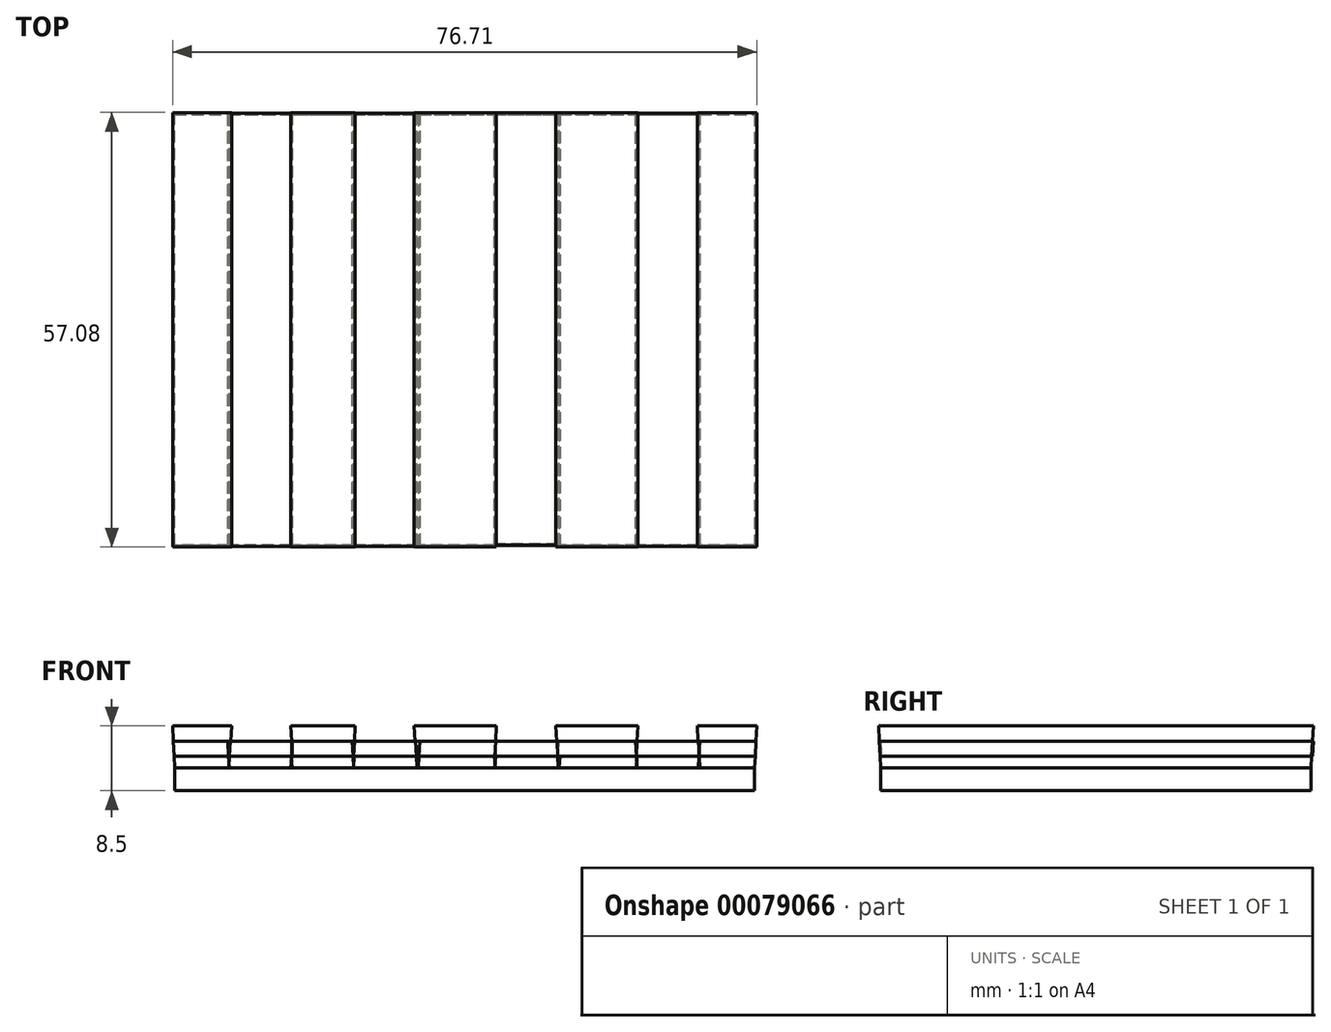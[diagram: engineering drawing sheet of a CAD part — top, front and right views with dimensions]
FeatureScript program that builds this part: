
annotation { "Feature Type Name" : "Feature", "Feature Type Description" : "" }
export const myFeature = defineFeature(function(context is Context, id is Id, definition is map)
    precondition{}
    {
        {
            var Q0;
            Q0=qCreatedBy(makeId("Top.planeOp"),FACE);
            var sketch = newSketch(context, id + "F0", { "sketchPlane" : qUnion([Q0])});
            skLineSegment(sketch, "E0.bottom", {"start": v(-76.14, 56.5) * mm, "end": v(0, 56.5) * mm});
            skLineSegment(sketch, "E0.top", {"start": v(-76.14, 0) * mm, "end": v(0, 0) * mm});
            skLineSegment(sketch, "E0.left", {"start": v(-76.14, 56.5) * mm, "end": v(-76.14, 0) * mm});
            skLineSegment(sketch, "E0.right", {"start": v(0, 56.5) * mm, "end": v(0, 0) * mm});
            skSolve(sketch);
        }
        {
            var Q0;
            Q0=qSketchRegion(id+"F0",true);
            extrude(context, id + "F1", {"entities" : qUnion([Q0]), "depth" : 3 * mm});
        }
        {
            var Q0;
            Q0=makeQuery(id+"F1.opExtrude","CAP_FACE",FACE,{"disambiguationData":[OSD([sQuery(id+"F0.wireOp",EDGE,"E0.bottom"),sQuery(id+"F0.wireOp",EDGE,"E0.top"),sQuery(id+"F0.wireOp",EDGE,"E0.left"),sQuery(id+"F0.wireOp",EDGE,"E0.right")])],"isStart":false});
            var sketch = newSketch(context, id + "F2", { "sketchPlane" : qUnion([Q0])});
            skLineSegment(sketch, "E1.bottom", {"start": v(-76.14, 56.5) * mm, "end": v(0, 56.5) * mm});
            skLineSegment(sketch, "E1.top", {"start": v(-76.14, 0) * mm, "end": v(0, 0) * mm});
            skLineSegment(sketch, "E1.left", {"start": v(-76.14, 56.5) * mm, "end": v(-76.14, 0) * mm});
            skLineSegment(sketch, "E1.right", {"start": v(0, 56.5) * mm, "end": v(0, 0) * mm});
            skSolve(sketch);
        }
        {
            var Q0;
            Q0=makeQuery(id+"F2.imprint","IMPRINT",FACE,{"disambiguationData":[TD([[makeQuery(id+"F2.imprint","IMPRINT",EDGE,{"derivedFrom":sQuery(id+"F2.wireOp",EDGE,"E1.bottom")}),-1.0]])]});
            extrude(context, id + "F3", {"entities" : qUnion([Q0]), "depth" : 1.5 * mm, "hasDraft" : true, "draftAngle" : 3 * degree});
        }
        {
            var Q0;
            Q0=makeQuery(id+"F3.opExtrude","CAP_FACE",FACE,{"disambiguationData":[OSD([sQuery(id+"F2.wireOp",EDGE,"E1.bottom"),sQuery(id+"F2.wireOp",EDGE,"E1.top"),sQuery(id+"F2.wireOp",EDGE,"E1.left"),sQuery(id+"F2.wireOp",EDGE,"E1.right")])],"isStart":false});
            var sketch = newSketch(context, id + "F4", { "sketchPlane" : qUnion([Q0])});
            skLineSegment(sketch, "E2.bottom", {"start": v(-76.22, 56.58) * mm, "end": v(0.08, 56.58) * mm});
            skLineSegment(sketch, "E2.top", {"start": v(-76.22, -0.08) * mm, "end": v(0.08, -0.08) * mm});
            skLineSegment(sketch, "E2.left", {"start": v(-76.22, 56.58) * mm, "end": v(-76.22, -0.08) * mm});
            skLineSegment(sketch, "E2.right", {"start": v(0.08, 56.58) * mm, "end": v(0.08, -0.08) * mm});
            skSolve(sketch);
        }
        {
            var Q0;
            Q0=qSketchRegion(id+"F4",true);
            extrude(context, id + "F5", {"entities" : qUnion([Q0]), "depth" : 2 * mm, "hasDraft" : true, "draftAngle" : 3 * degree});
        }
        {
            var Q0;
            Q0=makeQuery(id+"F5.opExtrude","CAP_FACE",FACE,{"disambiguationData":[OSD([sQuery(id+"F4.wireOp",EDGE,"E2.bottom"),sQuery(id+"F4.wireOp",EDGE,"E2.top"),sQuery(id+"F4.wireOp",EDGE,"E2.left"),sQuery(id+"F4.wireOp",EDGE,"E2.right")])],"isStart":false});
            var sketch = newSketch(context, id + "F6", { "sketchPlane" : qUnion([Q0])});
            skLineSegment(sketch, "E3.bottom", {"start": v(-68.76, 56.68) * mm, "end": v(-60.82, 56.68) * mm});
            skLineSegment(sketch, "E3.top", {"start": v(-68.76, -0.18) * mm, "end": v(-60.82, -0.18) * mm});
            skLineSegment(sketch, "E3.left", {"start": v(-68.76, 56.68) * mm, "end": v(-68.76, -0.18) * mm});
            skLineSegment(sketch, "E3.right", {"start": v(-60.82, 56.68) * mm, "end": v(-60.82, -0.18) * mm});
            skSolve(sketch);
        }
        {
            var Q0;
            Q0=qSketchRegion(id+"F6",true);
            extrude(context, id + "F7", {"entities" : qUnion([Q0]), "operationType" : NewBodyOperationType.REMOVE, "oppositeDirection" : true, "depth" : 2 * mm, "hasDraft" : true, "draftAngle" : 3 * degree});
        }
        {
            var Q0;
            {var subQ0=sQuery(id+"F4.wireOp",EDGE,"E2.bottom");var subQ1=sQuery(id+"F4.wireOp",EDGE,"E2.top");var subQ2=sQuery(id+"F4.wireOp",EDGE,"E2.right");Q0=makeQuery(id+"F7.boolean.opBoolean","SPLIT",FACE,{"disambiguationData":[TD([makeQuery(id+"F5.opExtrude","SWEPT_FACE",FACE,{"disambiguationData":[OSD([subQ2])]})])],"derivedFrom":makeQuery(id+"F5.opExtrude","CAP_FACE",FACE,{"disambiguationData":[OSD([subQ0,subQ1,sQuery(id+"F4.wireOp",EDGE,"E2.left"),subQ2])],"isStart":false})});}
            var sketch = newSketch(context, id + "F8", { "sketchPlane" : qUnion([Q0])});
            skLineSegment(sketch, "E4.bottom", {"start": v(-52.56, 56.68) * mm, "end": v(-44.62, 56.68) * mm});
            skLineSegment(sketch, "E4.top", {"start": v(-52.56, -0.18) * mm, "end": v(-44.62, -0.18) * mm});
            skLineSegment(sketch, "E4.left", {"start": v(-52.56, 56.68) * mm, "end": v(-52.56, -0.18) * mm});
            skLineSegment(sketch, "E4.right", {"start": v(-44.62, 56.68) * mm, "end": v(-44.62, -0.18) * mm});
            skSolve(sketch);
        }
        {
            var Q0;
            Q0=qSketchRegion(id+"F8",true);
            extrude(context, id + "F9", {"entities" : qUnion([Q0]), "operationType" : NewBodyOperationType.REMOVE, "oppositeDirection" : true, "depth" : 2 * mm, "hasDraft" : true, "draftAngle" : 3 * degree});
        }
        {
            var Q0;
            {var subQ0=sQuery(id+"F4.wireOp",EDGE,"E2.bottom");var subQ2=sQuery(id+"F4.wireOp",EDGE,"E2.top");var subQ4=sQuery(id+"F4.wireOp",EDGE,"E2.right");var subQ5=makeQuery(id+"F5.opExtrude","SWEPT_FACE",FACE,{"disambiguationData":[OSD([subQ4])]});Q0=makeQuery(id+"F9.boolean.opBoolean","SPLIT",FACE,{"disambiguationData":[TD([subQ5])],"derivedFrom":makeQuery(id+"F7.boolean.opBoolean","SPLIT",FACE,{"disambiguationData":[TD([subQ5])],"derivedFrom":makeQuery(id+"F5.opExtrude","CAP_FACE",FACE,{"disambiguationData":[OSD([subQ0,subQ2,sQuery(id+"F4.wireOp",EDGE,"E2.left"),subQ4])],"isStart":false})})});}
            var sketch = newSketch(context, id + "F10", { "sketchPlane" : qUnion([Q0])});
            skLineSegment(sketch, "E5.bottom", {"start": v(-34, 56.68) * mm, "end": v(-25.99, 56.68) * mm});
            skLineSegment(sketch, "E5.top", {"start": v(-34, -0.18) * mm, "end": v(-25.99, -0.18) * mm});
            skLineSegment(sketch, "E5.left", {"start": v(-34, 56.68) * mm, "end": v(-34, -0.18) * mm});
            skLineSegment(sketch, "E5.right", {"start": v(-25.99, 56.68) * mm, "end": v(-25.99, -0.18) * mm});
            skSolve(sketch);
        }
        {
            var Q0;
            Q0=qSketchRegion(id+"F10",true);
            extrude(context, id + "F11", {"entities" : qUnion([Q0]), "operationType" : NewBodyOperationType.REMOVE, "oppositeDirection" : true, "depth" : 2 * mm, "hasDraft" : true, "draftAngle" : 3 * degree});
        }
        {
            var Q0;
            {var subQ0=sQuery(id+"F4.wireOp",EDGE,"E2.bottom");var subQ2=sQuery(id+"F4.wireOp",EDGE,"E2.top");var subQ4=sQuery(id+"F4.wireOp",EDGE,"E2.right");var subQ5=makeQuery(id+"F5.opExtrude","SWEPT_FACE",FACE,{"disambiguationData":[OSD([subQ4])]});Q0=makeQuery(id+"F11.boolean.opBoolean","SPLIT",FACE,{"disambiguationData":[TD([subQ5])],"derivedFrom":makeQuery(id+"F9.boolean.opBoolean","SPLIT",FACE,{"disambiguationData":[TD([subQ5])],"derivedFrom":makeQuery(id+"F7.boolean.opBoolean","SPLIT",FACE,{"disambiguationData":[TD([subQ5])],"derivedFrom":makeQuery(id+"F5.opExtrude","CAP_FACE",FACE,{"disambiguationData":[OSD([subQ0,subQ2,sQuery(id+"F4.wireOp",EDGE,"E2.left"),subQ4])],"isStart":false})})})});}
            var sketch = newSketch(context, id + "F12", { "sketchPlane" : qUnion([Q0])});
            skLineSegment(sketch, "E6.bottom", {"start": v(-15.44, 56.68) * mm, "end": v(-7.42, 56.68) * mm});
            skLineSegment(sketch, "E6.top", {"start": v(-15.44, -0.18) * mm, "end": v(-7.42, -0.18) * mm});
            skLineSegment(sketch, "E6.left", {"start": v(-15.44, 56.68) * mm, "end": v(-15.44, -0.18) * mm});
            skLineSegment(sketch, "E6.right", {"start": v(-7.42, 56.68) * mm, "end": v(-7.42, -0.18) * mm});
            skSolve(sketch);
        }
        {
            var Q0;
            Q0=qSketchRegion(id+"F12",true);
            extrude(context, id + "F13", {"entities" : qUnion([Q0]), "operationType" : NewBodyOperationType.REMOVE, "oppositeDirection" : true, "depth" : 2 * mm, "hasDraft" : true, "draftAngle" : 3 * degree});
        }
        {
            var Q0;
            {var subQ0=sQuery(id+"F4.wireOp",EDGE,"E2.bottom");var subQ1=sQuery(id+"F4.wireOp",EDGE,"E2.top");var subQ2=sQuery(id+"F4.wireOp",EDGE,"E2.left");Q0=makeQuery(id+"F7.boolean.opBoolean","SPLIT",FACE,{"disambiguationData":[TD([makeQuery(id+"F5.opExtrude","SWEPT_FACE",FACE,{"disambiguationData":[OSD([subQ2])]})])],"derivedFrom":makeQuery(id+"F5.opExtrude","CAP_FACE",FACE,{"disambiguationData":[OSD([subQ0,subQ1,subQ2,sQuery(id+"F4.wireOp",EDGE,"E2.right")])],"isStart":false})});}
            var sketch = newSketch(context, id + "F14", { "sketchPlane" : qUnion([Q0])});
            skLineSegment(sketch, "E7.bottom", {"start": v(-76.32, 56.68) * mm, "end": v(-68.76, 56.68) * mm});
            skLineSegment(sketch, "E7.top", {"start": v(-76.32, -0.18) * mm, "end": v(-68.76, -0.18) * mm});
            skLineSegment(sketch, "E7.left", {"start": v(-76.32, 56.68) * mm, "end": v(-76.32, -0.18) * mm});
            skLineSegment(sketch, "E7.right", {"start": v(-68.76, 56.68) * mm, "end": v(-68.76, -0.18) * mm});
            skSolve(sketch);
        }
        {
            var Q0;
            Q0=qSketchRegion(id+"F14",true);
            extrude(context, id + "F15", {"entities" : qUnion([Q0]), "depth" : 2 * mm, "hasDraft" : true, "draftAngle" : 3 * degree});
        }
        {
            var Q0;
            {var subQ0=sQuery(id+"F4.wireOp",EDGE,"E2.bottom");var subQ2=sQuery(id+"F4.wireOp",EDGE,"E2.top");var subQ4=makeQuery(id+"F7.opExtrude","SWEPT_FACE",FACE,{"disambiguationData":[OSD([sQuery(id+"F6.wireOp",EDGE,"E3.right")])]});var subQ5=sQuery(id+"F4.wireOp",EDGE,"E2.right");Q0=makeQuery(id+"F9.boolean.opBoolean","SPLIT",FACE,{"disambiguationData":[TD([makeQuery(id+"F7.boolean.opBoolean","COPY",FACE,{"derivedFrom":subQ4})])],"derivedFrom":makeQuery(id+"F7.boolean.opBoolean","SPLIT",FACE,{"disambiguationData":[TD([makeQuery(id+"F5.opExtrude","SWEPT_FACE",FACE,{"disambiguationData":[OSD([subQ5])]})])],"derivedFrom":makeQuery(id+"F5.opExtrude","CAP_FACE",FACE,{"disambiguationData":[OSD([subQ0,subQ2,sQuery(id+"F4.wireOp",EDGE,"E2.left"),subQ5])],"isStart":false})})});}
            var sketch = newSketch(context, id + "F16", { "sketchPlane" : qUnion([Q0])});
            skLineSegment(sketch, "E8.bottom", {"start": v(-60.82, 56.68) * mm, "end": v(-52.56, 56.68) * mm});
            skLineSegment(sketch, "E8.top", {"start": v(-60.82, -0.18) * mm, "end": v(-52.56, -0.18) * mm});
            skLineSegment(sketch, "E8.left", {"start": v(-60.82, 56.68) * mm, "end": v(-60.82, -0.18) * mm});
            skLineSegment(sketch, "E8.right", {"start": v(-52.56, 56.68) * mm, "end": v(-52.56, -0.18) * mm});
            skSolve(sketch);
        }
        {
            var Q0;
            Q0=qSketchRegion(id+"F16",true);
            extrude(context, id + "F17", {"entities" : qUnion([Q0]), "depth" : 2 * mm, "hasDraft" : true, "draftAngle" : 3 * degree});
        }
        {
            var Q0;
            Q0=makeQuery(id+"F3.opExtrude","CAP_FACE",FACE,{"disambiguationData":[OSD([sQuery(id+"F2.wireOp",EDGE,"E1.bottom"),sQuery(id+"F2.wireOp",EDGE,"E1.top"),sQuery(id+"F2.wireOp",EDGE,"E1.left"),sQuery(id+"F2.wireOp",EDGE,"E1.right")])],"isStart":false});
            var sketch = newSketch(context, id + "F18", { "sketchPlane" : qUnion([Q0])});
            skLineSegment(sketch, "E9.bottom", {"start": v(-68.78, 56.58) * mm, "end": v(-61.04, 56.58) * mm});
            skLineSegment(sketch, "E9.top", {"start": v(-68.78, -0.08) * mm, "end": v(-61.04, -0.08) * mm});
            skLineSegment(sketch, "E9.left", {"start": v(-68.78, 56.58) * mm, "end": v(-68.78, -0.08) * mm});
            skLineSegment(sketch, "E9.right", {"start": v(-61.04, 56.58) * mm, "end": v(-61.04, -0.08) * mm});
            skSolve(sketch);
        }
        {
            var Q0;
            Q0=qSketchRegion(id+"F18",true);
            extrude(context, id + "F19", {"entities" : qUnion([Q0]), "depth" : 2 * mm, "hasDraft" : true, "draftAngle" : 3 * degree});
        }
        {
            var Q0;
            Q0=makeQuery(id+"F3.opExtrude","CAP_FACE",FACE,{"disambiguationData":[OSD([sQuery(id+"F2.wireOp",EDGE,"E1.bottom"),sQuery(id+"F2.wireOp",EDGE,"E1.top"),sQuery(id+"F2.wireOp",EDGE,"E1.left"),sQuery(id+"F2.wireOp",EDGE,"E1.right")])],"isStart":false});
            var sketch = newSketch(context, id + "F20", { "sketchPlane" : qUnion([Q0])});
            skLineSegment(sketch, "E10.bottom", {"start": v(-52.37, 56.58) * mm, "end": v(-44.62, 56.58) * mm});
            skLineSegment(sketch, "E10.top", {"start": v(-52.37, -0.08) * mm, "end": v(-44.62, -0.08) * mm});
            skLineSegment(sketch, "E10.left", {"start": v(-52.37, 56.58) * mm, "end": v(-52.37, -0.08) * mm});
            skLineSegment(sketch, "E10.right", {"start": v(-44.62, 56.58) * mm, "end": v(-44.62, -0.08) * mm});
            skSolve(sketch);
        }
        {
            var Q0;
            Q0=qSketchRegion(id+"F20",true);
            extrude(context, id + "F21", {"entities" : qUnion([Q0]), "depth" : 2 * mm, "hasDraft" : true, "draftAngle" : 3 * degree});
        }
        {
            var Q0;
            {var subQ0=sQuery(id+"F4.wireOp",EDGE,"E2.bottom");var subQ2=sQuery(id+"F4.wireOp",EDGE,"E2.top");var subQ4=makeQuery(id+"F9.opExtrude","SWEPT_FACE",FACE,{"disambiguationData":[OSD([sQuery(id+"F8.wireOp",EDGE,"E4.right")])]});var subQ5=sQuery(id+"F4.wireOp",EDGE,"E2.right");var subQ6=makeQuery(id+"F5.opExtrude","SWEPT_FACE",FACE,{"disambiguationData":[OSD([subQ5])]});Q0=makeQuery(id+"F11.boolean.opBoolean","SPLIT",FACE,{"disambiguationData":[TD([makeQuery(id+"F9.boolean.opBoolean","COPY",FACE,{"derivedFrom":subQ4})])],"derivedFrom":makeQuery(id+"F9.boolean.opBoolean","SPLIT",FACE,{"disambiguationData":[TD([subQ6])],"derivedFrom":makeQuery(id+"F7.boolean.opBoolean","SPLIT",FACE,{"disambiguationData":[TD([subQ6])],"derivedFrom":makeQuery(id+"F5.opExtrude","CAP_FACE",FACE,{"disambiguationData":[OSD([subQ0,subQ2,sQuery(id+"F4.wireOp",EDGE,"E2.left"),subQ5])],"isStart":false})})})});}
            var sketch = newSketch(context, id + "F22", { "sketchPlane" : qUnion([Q0])});
            skLineSegment(sketch, "E11.bottom", {"start": v(-44.62, 56.68) * mm, "end": v(-34, 56.68) * mm});
            skLineSegment(sketch, "E11.top", {"start": v(-44.62, -0.18) * mm, "end": v(-34, -0.18) * mm});
            skLineSegment(sketch, "E11.left", {"start": v(-44.62, 56.68) * mm, "end": v(-44.62, -0.18) * mm});
            skLineSegment(sketch, "E11.right", {"start": v(-34, 56.68) * mm, "end": v(-34, -0.18) * mm});
            skSolve(sketch);
        }
        {
            var Q0;
            Q0=qSketchRegion(id+"F22",true);
            extrude(context, id + "F23", {"entities" : qUnion([Q0]), "depth" : 2 * mm, "hasDraft" : true, "draftAngle" : 3 * degree});
        }
        {
            var Q0;
            Q0=makeQuery(id+"F3.opExtrude","CAP_FACE",FACE,{"disambiguationData":[OSD([sQuery(id+"F2.wireOp",EDGE,"E1.bottom"),sQuery(id+"F2.wireOp",EDGE,"E1.top"),sQuery(id+"F2.wireOp",EDGE,"E1.left"),sQuery(id+"F2.wireOp",EDGE,"E1.right")])],"isStart":false});
            var sketch = newSketch(context, id + "F24", { "sketchPlane" : qUnion([Q0])});
            skLineSegment(sketch, "E12.bottom", {"start": v(-33.8, 56.58) * mm, "end": v(-26.06, 56.58) * mm});
            skLineSegment(sketch, "E12.top", {"start": v(-33.8, -0.08) * mm, "end": v(-26.06, -0.08) * mm});
            skLineSegment(sketch, "E12.left", {"start": v(-33.8, 56.58) * mm, "end": v(-33.8, -0.08) * mm});
            skLineSegment(sketch, "E12.right", {"start": v(-26.06, 56.58) * mm, "end": v(-26.06, -0.08) * mm});
            skSolve(sketch);
        }
        {
            var Q0;
            Q0=qSketchRegion(id+"F24",true);
            extrude(context, id + "F25", {"entities" : qUnion([Q0]), "depth" : 2 * mm, "hasDraft" : true, "draftAngle" : 3 * degree});
        }
        {
            var Q0;
            {var subQ0=sQuery(id+"F4.wireOp",EDGE,"E2.bottom");var subQ2=sQuery(id+"F4.wireOp",EDGE,"E2.top");var subQ4=makeQuery(id+"F11.opExtrude","SWEPT_FACE",FACE,{"disambiguationData":[OSD([sQuery(id+"F10.wireOp",EDGE,"E5.right")])]});var subQ5=sQuery(id+"F4.wireOp",EDGE,"E2.right");var subQ6=makeQuery(id+"F5.opExtrude","SWEPT_FACE",FACE,{"disambiguationData":[OSD([subQ5])]});Q0=makeQuery(id+"F13.boolean.opBoolean","SPLIT",FACE,{"disambiguationData":[TD([makeQuery(id+"F11.boolean.opBoolean","COPY",FACE,{"derivedFrom":subQ4})])],"derivedFrom":makeQuery(id+"F11.boolean.opBoolean","SPLIT",FACE,{"disambiguationData":[TD([subQ6])],"derivedFrom":makeQuery(id+"F9.boolean.opBoolean","SPLIT",FACE,{"disambiguationData":[TD([subQ6])],"derivedFrom":makeQuery(id+"F7.boolean.opBoolean","SPLIT",FACE,{"disambiguationData":[TD([subQ6])],"derivedFrom":makeQuery(id+"F5.opExtrude","CAP_FACE",FACE,{"disambiguationData":[OSD([subQ0,subQ2,sQuery(id+"F4.wireOp",EDGE,"E2.left"),subQ5])],"isStart":false})})})})});}
            var sketch = newSketch(context, id + "F26", { "sketchPlane" : qUnion([Q0])});
            skLineSegment(sketch, "E13.bottom", {"start": v(-25.99, 56.68) * mm, "end": v(-15.44, 56.68) * mm});
            skLineSegment(sketch, "E13.top", {"start": v(-25.99, -0.18) * mm, "end": v(-15.44, -0.18) * mm});
            skLineSegment(sketch, "E13.left", {"start": v(-25.99, 56.68) * mm, "end": v(-25.99, -0.18) * mm});
            skLineSegment(sketch, "E13.right", {"start": v(-15.44, 56.68) * mm, "end": v(-15.44, -0.18) * mm});
            skSolve(sketch);
        }
        {
            var Q0;
            Q0=qSketchRegion(id+"F26",true);
            extrude(context, id + "F27", {"entities" : qUnion([Q0]), "depth" : 2 * mm, "hasDraft" : true, "draftAngle" : 3 * degree});
        }
        {
            var Q0;
            Q0=makeQuery(id+"F3.opExtrude","CAP_FACE",FACE,{"disambiguationData":[OSD([sQuery(id+"F2.wireOp",EDGE,"E1.bottom"),sQuery(id+"F2.wireOp",EDGE,"E1.top"),sQuery(id+"F2.wireOp",EDGE,"E1.left"),sQuery(id+"F2.wireOp",EDGE,"E1.right")])],"isStart":false});
            var sketch = newSketch(context, id + "F28", { "sketchPlane" : qUnion([Q0])});
            skLineSegment(sketch, "E14.bottom", {"start": v(-15.24, 56.58) * mm, "end": v(-7.49, 56.58) * mm});
            skLineSegment(sketch, "E14.top", {"start": v(-15.24, -0.08) * mm, "end": v(-7.49, -0.08) * mm});
            skLineSegment(sketch, "E14.left", {"start": v(-15.24, 56.58) * mm, "end": v(-15.24, -0.08) * mm});
            skLineSegment(sketch, "E14.right", {"start": v(-7.49, 56.58) * mm, "end": v(-7.49, -0.08) * mm});
            skSolve(sketch);
        }
        {
            var Q0;
            Q0=qSketchRegion(id+"F28",true);
            extrude(context, id + "F29", {"entities" : qUnion([Q0]), "depth" : 2 * mm, "hasDraft" : true, "draftAngle" : 3 * degree});
        }
        {
            var Q0;
            {var subQ0=sQuery(id+"F4.wireOp",EDGE,"E2.bottom");var subQ2=sQuery(id+"F4.wireOp",EDGE,"E2.top");var subQ4=sQuery(id+"F4.wireOp",EDGE,"E2.right");var subQ5=makeQuery(id+"F5.opExtrude","SWEPT_FACE",FACE,{"disambiguationData":[OSD([subQ4])]});Q0=makeQuery(id+"F13.boolean.opBoolean","SPLIT",FACE,{"disambiguationData":[TD([subQ5])],"derivedFrom":makeQuery(id+"F11.boolean.opBoolean","SPLIT",FACE,{"disambiguationData":[TD([subQ5])],"derivedFrom":makeQuery(id+"F9.boolean.opBoolean","SPLIT",FACE,{"disambiguationData":[TD([subQ5])],"derivedFrom":makeQuery(id+"F7.boolean.opBoolean","SPLIT",FACE,{"disambiguationData":[TD([subQ5])],"derivedFrom":makeQuery(id+"F5.opExtrude","CAP_FACE",FACE,{"disambiguationData":[OSD([subQ0,subQ2,sQuery(id+"F4.wireOp",EDGE,"E2.left"),subQ4])],"isStart":false})})})})});}
            var sketch = newSketch(context, id + "F30", { "sketchPlane" : qUnion([Q0])});
            skLineSegment(sketch, "E15.bottom", {"start": v(-7.42, 56.68) * mm, "end": v(0.18, 56.68) * mm});
            skLineSegment(sketch, "E15.top", {"start": v(-7.42, -0.18) * mm, "end": v(0.18, -0.18) * mm});
            skLineSegment(sketch, "E15.left", {"start": v(-7.42, 56.68) * mm, "end": v(-7.42, -0.18) * mm});
            skLineSegment(sketch, "E15.right", {"start": v(0.18, 56.68) * mm, "end": v(0.18, -0.18) * mm});
            skSolve(sketch);
        }
        {
            var Q0;
            Q0=qSketchRegion(id+"F30",true);
            extrude(context, id + "F31", {"entities" : qUnion([Q0]), "depth" : 2 * mm, "hasDraft" : true, "draftAngle" : 3 * degree});
        }
        {
            var Q0;
            Q0=makeQuery(id+"F19.opExtrude","CAP_FACE",FACE,{"disambiguationData":[OSD([sQuery(id+"F18.wireOp",EDGE,"E9.bottom"),sQuery(id+"F18.wireOp",EDGE,"E9.top"),sQuery(id+"F18.wireOp",EDGE,"E9.left"),sQuery(id+"F18.wireOp",EDGE,"E9.right")])],"isStart":false});
            extrude(context, id + "F32", {"entities" : qUnion([Q0]), "operationType" : NewBodyOperationType.REMOVE, "oppositeDirection" : true, "depth" : 3.5 * mm, "hasDraft" : true, "draftAngle" : 3 * degree});
        }
        {
            var Q0;
            Q0=makeQuery(id+"F21.opExtrude","CAP_FACE",FACE,{"disambiguationData":[OSD([sQuery(id+"F20.wireOp",EDGE,"E10.bottom"),sQuery(id+"F20.wireOp",EDGE,"E10.top"),sQuery(id+"F20.wireOp",EDGE,"E10.left"),sQuery(id+"F20.wireOp",EDGE,"E10.right")])],"isStart":false});
            extrude(context, id + "F33", {"entities" : qUnion([Q0]), "operationType" : NewBodyOperationType.REMOVE, "oppositeDirection" : true, "depth" : 3.5 * mm, "hasDraft" : true, "draftAngle" : 3 * degree});
        }
        {
            var Q0;
            Q0=makeQuery(id+"F25.opExtrude","CAP_FACE",FACE,{"disambiguationData":[OSD([sQuery(id+"F24.wireOp",EDGE,"E12.bottom"),sQuery(id+"F24.wireOp",EDGE,"E12.top"),sQuery(id+"F24.wireOp",EDGE,"E12.left"),sQuery(id+"F24.wireOp",EDGE,"E12.right")])],"isStart":false});
            extrude(context, id + "F34", {"entities" : qUnion([Q0]), "operationType" : NewBodyOperationType.REMOVE, "oppositeDirection" : true, "depth" : 3.5 * mm, "hasDraft" : true, "draftAngle" : 3 * degree});
        }
        {
            var Q0;
            Q0=makeQuery(id+"F29.opExtrude","CAP_FACE",FACE,{"disambiguationData":[OSD([sQuery(id+"F28.wireOp",EDGE,"E14.bottom"),sQuery(id+"F28.wireOp",EDGE,"E14.top"),sQuery(id+"F28.wireOp",EDGE,"E14.left"),sQuery(id+"F28.wireOp",EDGE,"E14.right")])],"isStart":false});
            extrude(context, id + "F35", {"entities" : qUnion([Q0]), "operationType" : NewBodyOperationType.REMOVE, "oppositeDirection" : true, "depth" : 3.5 * mm, "hasDraft" : true, "draftAngle" : 3 * degree});
        }
        {
            var Q0;
            Q0=makeQuery(id+"F1.opExtrude","CAP_FACE",FACE,{"disambiguationData":[OSD([sQuery(id+"F0.wireOp",EDGE,"E0.bottom"),sQuery(id+"F0.wireOp",EDGE,"E0.top"),sQuery(id+"F0.wireOp",EDGE,"E0.left"),sQuery(id+"F0.wireOp",EDGE,"E0.right")])],"isStart":false});
            var sketch = newSketch(context, id + "F36", { "sketchPlane" : qUnion([Q0])});
            skLineSegment(sketch, "E16.bottom", {"start": v(-69.13, 56.5) * mm, "end": v(-60.43, 56.5) * mm});
            skLineSegment(sketch, "E16.top", {"start": v(-69.13, 0) * mm, "end": v(-60.43, 0) * mm});
            skLineSegment(sketch, "E16.left", {"start": v(-69.13, 56.5) * mm, "end": v(-69.13, 0) * mm});
            skLineSegment(sketch, "E16.right", {"start": v(-60.43, 56.5) * mm, "end": v(-60.43, 0) * mm});
            skSolve(sketch);
        }
        {
            var Q0;
            Q0=qSketchRegion(id+"F36",true);
            extrude(context, id + "F37", {"entities" : qUnion([Q0]), "depth" : 1.5 * mm, "hasDraft" : true, "draftAngle" : 3 * degree});
        }
        {
            var Q0;
            Q0=makeQuery(id+"F1.opExtrude","CAP_FACE",FACE,{"disambiguationData":[OSD([sQuery(id+"F0.wireOp",EDGE,"E0.bottom"),sQuery(id+"F0.wireOp",EDGE,"E0.top"),sQuery(id+"F0.wireOp",EDGE,"E0.left"),sQuery(id+"F0.wireOp",EDGE,"E0.right")])],"isStart":false});
            var sketch = newSketch(context, id + "F38", { "sketchPlane" : qUnion([Q0])});
            skLineSegment(sketch, "E17.bottom", {"start": v(-52.5, 56.5) * mm, "end": v(-44.3, 56.5) * mm});
            skLineSegment(sketch, "E17.top", {"start": v(-52.5, 0) * mm, "end": v(-44.3, 0) * mm});
            skLineSegment(sketch, "E17.left", {"start": v(-52.5, 56.5) * mm, "end": v(-52.5, 0) * mm});
            skLineSegment(sketch, "E17.right", {"start": v(-44.3, 56.5) * mm, "end": v(-44.3, 0) * mm});
            skSolve(sketch);
        }
        {
            var Q0;
            Q0=qSketchRegion(id+"F38",true);
            extrude(context, id + "F39", {"entities" : qUnion([Q0]), "depth" : 1.5 * mm, "hasDraft" : true, "draftAngle" : 3 * degree});
        }
        {
            var Q0;
            Q0=makeQuery(id+"F37.opExtrude","SWEPT_BODY",BODY,{"disambiguationData":[OSD([sQuery(id+"F36.wireOp",EDGE,"E16.bottom"),sQuery(id+"F36.wireOp",EDGE,"E16.top"),sQuery(id+"F36.wireOp",EDGE,"E16.left"),sQuery(id+"F36.wireOp",EDGE,"E16.right")])]});
            deleteBodies(context, id + "F40", {"entities" : qUnion([Q0])});
        }
        {
            var Q0;
            Q0=makeQuery(id+"F39.opExtrude","SWEPT_BODY",BODY,{"disambiguationData":[OSD([sQuery(id+"F38.wireOp",EDGE,"E17.bottom"),sQuery(id+"F38.wireOp",EDGE,"E17.top"),sQuery(id+"F38.wireOp",EDGE,"E17.left"),sQuery(id+"F38.wireOp",EDGE,"E17.right")])]});
            deleteBodies(context, id + "F41", {"entities" : qUnion([Q0])});
        }
        {
            var Q0;
            Q0=makeQuery(id+"F1.opExtrude","CAP_FACE",FACE,{"disambiguationData":[OSD([sQuery(id+"F0.wireOp",EDGE,"E0.bottom"),sQuery(id+"F0.wireOp",EDGE,"E0.top"),sQuery(id+"F0.wireOp",EDGE,"E0.left"),sQuery(id+"F0.wireOp",EDGE,"E0.right")])],"isStart":false});
            var sketch = newSketch(context, id + "F42", { "sketchPlane" : qUnion([Q0])});
            skLineSegment(sketch, "E18.bottom", {"start": v(-69, 56.5) * mm, "end": v(-60.9, 56.5) * mm});
            skLineSegment(sketch, "E18.top", {"start": v(-69, 0) * mm, "end": v(-60.9, 0) * mm});
            skLineSegment(sketch, "E18.left", {"start": v(-69, 56.5) * mm, "end": v(-69, 0) * mm});
            skLineSegment(sketch, "E18.right", {"start": v(-60.9, 56.5) * mm, "end": v(-60.9, 0) * mm});
            skSolve(sketch);
        }
        {
            var Q0;
            Q0=qSketchRegion(id+"F42",true);
            extrude(context, id + "F43", {"entities" : qUnion([Q0]), "depth" : 1.5 * mm, "hasDraft" : true, "draftAngle" : 3 * degree});
        }
        {
            var Q0;
            Q0=makeQuery(id+"F1.opExtrude","CAP_FACE",FACE,{"disambiguationData":[OSD([sQuery(id+"F0.wireOp",EDGE,"E0.bottom"),sQuery(id+"F0.wireOp",EDGE,"E0.top"),sQuery(id+"F0.wireOp",EDGE,"E0.left"),sQuery(id+"F0.wireOp",EDGE,"E0.right")])],"isStart":false});
            var sketch = newSketch(context, id + "F44", { "sketchPlane" : qUnion([Q0])});
            skLineSegment(sketch, "E19.bottom", {"start": v(-52.66, 56.5) * mm, "end": v(-44.15, 56.5) * mm});
            skLineSegment(sketch, "E19.top", {"start": v(-52.66, 0) * mm, "end": v(-44.15, 0) * mm});
            skLineSegment(sketch, "E19.left", {"start": v(-52.66, 56.5) * mm, "end": v(-52.66, 0) * mm});
            skLineSegment(sketch, "E19.right", {"start": v(-44.15, 56.5) * mm, "end": v(-44.15, 0) * mm});
            skSolve(sketch);
        }
        {
            var Q0;
            Q0=qSketchRegion(id+"F44",true);
            extrude(context, id + "F45", {"entities" : qUnion([Q0]), "depth" : 1.5 * mm, "hasDraft" : true, "draftAngle" : 3 * degree});
        }
        {
            var Q0;
            Q0=makeQuery(id+"F1.opExtrude","CAP_FACE",FACE,{"disambiguationData":[OSD([sQuery(id+"F0.wireOp",EDGE,"E0.bottom"),sQuery(id+"F0.wireOp",EDGE,"E0.top"),sQuery(id+"F0.wireOp",EDGE,"E0.left"),sQuery(id+"F0.wireOp",EDGE,"E0.right")])],"isStart":false});
            var sketch = newSketch(context, id + "F46", { "sketchPlane" : qUnion([Q0])});
            skLineSegment(sketch, "E20.bottom", {"start": v(-34.07, 56.5) * mm, "end": v(-25.65, 56.5) * mm});
            skLineSegment(sketch, "E20.top", {"start": v(-34.07, 0) * mm, "end": v(-25.65, 0) * mm});
            skLineSegment(sketch, "E20.left", {"start": v(-34.07, 56.5) * mm, "end": v(-34.07, 0) * mm});
            skLineSegment(sketch, "E20.right", {"start": v(-25.65, 56.5) * mm, "end": v(-25.65, 0) * mm});
            skSolve(sketch);
        }
        {
            var Q0;
            Q0=qSketchRegion(id+"F46",true);
            extrude(context, id + "F47", {"entities" : qUnion([Q0]), "depth" : 1.5 * mm, "hasDraft" : true, "draftAngle" : 3 * degree});
        }
        {
            var Q0;
            Q0=makeQuery(id+"F1.opExtrude","CAP_FACE",FACE,{"disambiguationData":[OSD([sQuery(id+"F0.wireOp",EDGE,"E0.bottom"),sQuery(id+"F0.wireOp",EDGE,"E0.top"),sQuery(id+"F0.wireOp",EDGE,"E0.left"),sQuery(id+"F0.wireOp",EDGE,"E0.right")])],"isStart":false});
            var sketch = newSketch(context, id + "F48", { "sketchPlane" : qUnion([Q0])});
            skLineSegment(sketch, "E21.bottom", {"start": v(-15.42, 56.5) * mm, "end": v(-7.37, 56.5) * mm});
            skLineSegment(sketch, "E21.top", {"start": v(-15.42, 0) * mm, "end": v(-7.37, 0) * mm});
            skLineSegment(sketch, "E21.left", {"start": v(-15.42, 56.5) * mm, "end": v(-15.42, 0) * mm});
            skLineSegment(sketch, "E21.right", {"start": v(-7.37, 56.5) * mm, "end": v(-7.37, 0) * mm});
            skSolve(sketch);
        }
        {
            var Q0;
            Q0=qSketchRegion(id+"F48",true);
            extrude(context, id + "F49", {"entities" : qUnion([Q0]), "depth" : 1.5 * mm, "hasDraft" : true, "draftAngle" : 3 * degree});
        }
        {
            var Q0;
            Q0=makeQuery(id+"F43.opExtrude","CAP_FACE",FACE,{"disambiguationData":[OSD([sQuery(id+"F42.wireOp",EDGE,"E18.bottom"),sQuery(id+"F42.wireOp",EDGE,"E18.top"),sQuery(id+"F42.wireOp",EDGE,"E18.left"),sQuery(id+"F42.wireOp",EDGE,"E18.right")])],"isStart":false});
            var sketch = newSketch(context, id + "F50", { "sketchPlane" : qUnion([Q0])});
            skLineSegment(sketch, "E22.bottom", {"start": v(-69.08, 56.58) * mm, "end": v(-60.82, 56.58) * mm});
            skLineSegment(sketch, "E22.top", {"start": v(-69.08, -0.08) * mm, "end": v(-60.82, -0.08) * mm});
            skLineSegment(sketch, "E22.left", {"start": v(-69.08, 56.58) * mm, "end": v(-69.08, -0.08) * mm});
            skLineSegment(sketch, "E22.right", {"start": v(-60.82, 56.58) * mm, "end": v(-60.82, -0.08) * mm});
            skSolve(sketch);
        }
        {
            var Q0;
            Q0 = qSketchRegion(id + "F50", true);
            extrude(context, id + "F51", {"entities" : qUnion([Q0]), "depth" : 2 * mm, "hasDraft" : true, "draftAngle" : 3 * degree});
        }
        {
            var Q0;
            Q0=makeQuery(id+"F45.opExtrude","CAP_FACE",FACE,{"disambiguationData":[OSD([sQuery(id+"F44.wireOp",EDGE,"E19.bottom"),sQuery(id+"F44.wireOp",EDGE,"E19.top"),sQuery(id+"F44.wireOp",EDGE,"E19.left"),sQuery(id+"F44.wireOp",EDGE,"E19.right")])],"isStart":false});
            var sketch = newSketch(context, id + "F52", { "sketchPlane" : qUnion([Q0])});
            skLineSegment(sketch, "E23.bottom", {"start": v(-52.74, 56.58) * mm, "end": v(-44.07, 56.58) * mm});
            skLineSegment(sketch, "E23.top", {"start": v(-52.74, -0.08) * mm, "end": v(-44.07, -0.08) * mm});
            skLineSegment(sketch, "E23.left", {"start": v(-52.74, 56.58) * mm, "end": v(-52.74, -0.08) * mm});
            skLineSegment(sketch, "E23.right", {"start": v(-44.07, 56.58) * mm, "end": v(-44.07, -0.08) * mm});
            skSolve(sketch);
        }
        {
            var Q0;
            Q0=makeQuery(id+"F52.imprint","IMPRINT",FACE,{"disambiguationData":[TD([[makeQuery(id+"F52.imprint","IMPRINT",EDGE,{"derivedFrom":sQuery(id+"F52.wireOp",EDGE,"E23.bottom")}),-1.0]])]});
            extrude(context, id + "F53", {"entities" : qUnion([Q0]), "depth" : 2 * mm, "hasDraft" : true, "draftAngle" : 3 * degree});
        }
        {
            var Q0;
            Q0=makeQuery(id+"F47.opExtrude","CAP_FACE",FACE,{"disambiguationData":[OSD([sQuery(id+"F46.wireOp",EDGE,"E20.bottom"),sQuery(id+"F46.wireOp",EDGE,"E20.top"),sQuery(id+"F46.wireOp",EDGE,"E20.left"),sQuery(id+"F46.wireOp",EDGE,"E20.right")])],"isStart":false});
            var sketch = newSketch(context, id + "F54", { "sketchPlane" : qUnion([Q0])});
            skLineSegment(sketch, "E24.bottom", {"start": v(-34.04, 56.68) * mm, "end": v(-25.84, 56.68) * mm});
            skLineSegment(sketch, "E24.top", {"start": v(-34.04, 0.1) * mm, "end": v(-25.84, 0.1) * mm});
            skLineSegment(sketch, "E24.left", {"start": v(-34.04, 56.68) * mm, "end": v(-34.04, 0.1) * mm});
            skLineSegment(sketch, "E24.right", {"start": v(-25.84, 56.68) * mm, "end": v(-25.84, 0.1) * mm});
            skSolve(sketch);
        }
        {
            var Q0;
            Q0 = qSketchRegion(id + "F54", true);
            extrude(context, id + "F55", {"entities" : qUnion([Q0]), "depth" : 2 * mm, "hasDraft" : true, "draftAngle" : 3 * degree});
        }
        {
            var Q0;
            Q0=makeQuery(id+"F49.opExtrude","CAP_FACE",FACE,{"disambiguationData":[OSD([sQuery(id+"F48.wireOp",EDGE,"E21.bottom"),sQuery(id+"F48.wireOp",EDGE,"E21.top"),sQuery(id+"F48.wireOp",EDGE,"E21.left"),sQuery(id+"F48.wireOp",EDGE,"E21.right")])],"isStart":false});
            var sketch = newSketch(context, id + "F56", { "sketchPlane" : qUnion([Q0])});
            skLineSegment(sketch, "E25.bottom", {"start": v(-15.5, 56.58) * mm, "end": v(-7.3, 56.58) * mm});
            skLineSegment(sketch, "E25.top", {"start": v(-15.5, -0.08) * mm, "end": v(-7.3, -0.08) * mm});
            skLineSegment(sketch, "E25.left", {"start": v(-15.5, 56.58) * mm, "end": v(-15.5, -0.08) * mm});
            skLineSegment(sketch, "E25.right", {"start": v(-7.3, 56.58) * mm, "end": v(-7.3, -0.08) * mm});
            skSolve(sketch);
        }
        {
            var Q0;
            Q0 = qSketchRegion(id + "F56", true);
            extrude(context, id + "F57", {"entities" : qUnion([Q0]), "depth" : 2 * mm, "hasDraft" : true, "draftAngle" : 3 * degree});
        }
    });
